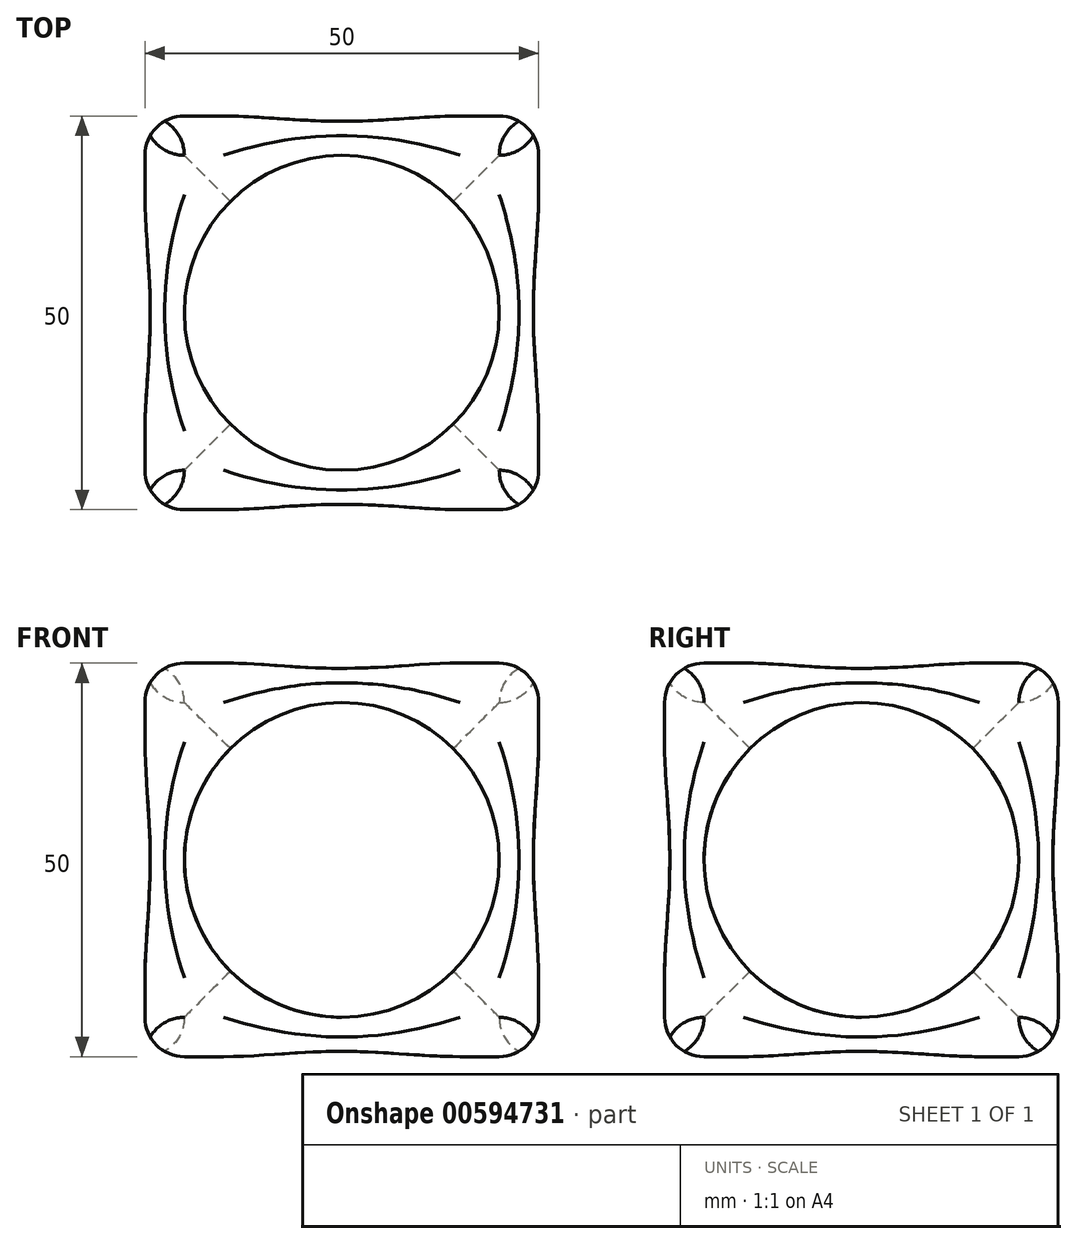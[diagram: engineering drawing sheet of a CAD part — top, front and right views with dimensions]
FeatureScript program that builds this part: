
annotation { "Feature Type Name" : "Feature", "Feature Type Description" : "" }
export const myFeature = defineFeature(function(context is Context, id is Id, definition is map)
    precondition{}
    {
        {
            var Q0;
            Q0=qCreatedBy(makeId("Top.planeOp"),FACE);
            var sketch = newSketch(context, id + "F0", { "sketchPlane" : qUnion([Q0])});
            skLineSegment(sketch, "E0.bottom", {"start": v(0, 0) * mm, "end": v(50, 0) * mm});
            skLineSegment(sketch, "E0.top", {"start": v(0, 50) * mm, "end": v(50, 50) * mm});
            skLineSegment(sketch, "E0.left", {"start": v(0, 0) * mm, "end": v(0, 50) * mm});
            skLineSegment(sketch, "E0.right", {"start": v(50, 0) * mm, "end": v(50, 50) * mm});
            skSolve(sketch);
        }
        {
            var Q0;
            Q0 = qSketchRegion(id + "F0", true);
            extrude(context, id + "F1", {"entities" : qUnion([Q0]), "depth" : 50 * mm, "offsetDistance" : 25 * mm});
        }
        {
            var Q0;
            Q0=makeQuery(id+"F1.opExtrude","SWEPT_FACE",FACE,{"disambiguationData":[OSD([sQuery(id+"F0.wireOp",EDGE,"E0.bottom")])]});
            var sketch = newSketch(context, id + "F2", { "sketchPlane" : qUnion([Q0])});
            skCircle(sketch, "E1", {"center": v(25, 25) * mm, "radius": 20 * mm});
            skSolve(sketch);
        }
        {
            var Q0;
            Q0=makeQuery(id+"F2.imprint","IMPRINT",FACE,{"disambiguationData":[TD([[makeQuery(id+"F2.imprint","IMPRINT",EDGE,{"derivedFrom":sQuery(id+"F2.wireOp",EDGE,"E1")}),1.0]])]});
            extrude(context, id + "F3", {"entities" : qUnion([Q0]), "operationType" : NewBodyOperationType.REMOVE, "oppositeDirection" : true, "depth" : 50 * mm, "offsetDistance" : 25 * mm});
        }
        {
            var Q0;
            Q0=makeQuery(id+"F1.opExtrude","SWEPT_FACE",FACE,{"disambiguationData":[OSD([sQuery(id+"F0.wireOp",EDGE,"E0.right")])]});
            var sketch = newSketch(context, id + "F4", { "sketchPlane" : qUnion([Q0])});
            skCircle(sketch, "E2", {"center": v(25, 25) * mm, "radius": 20 * mm});
            skSolve(sketch);
        }
        {
            var Q0;
            Q0=makeQuery(id+"F4.imprint","IMPRINT",FACE,{"disambiguationData":[TD([[makeQuery(id+"F4.imprint","IMPRINT",EDGE,{"derivedFrom":sQuery(id+"F4.wireOp",EDGE,"E2")}),1.0]])]});
            extrude(context, id + "F5", {"entities" : qUnion([Q0]), "operationType" : NewBodyOperationType.REMOVE, "oppositeDirection" : true, "depth" : 50 * mm, "offsetDistance" : 25 * mm});
        }
        {
            var Q0;
            Q0=makeQuery(id+"F1.opExtrude","CAP_FACE",FACE,{"disambiguationData":[OSD([sQuery(id+"F0.wireOp",EDGE,"E0.bottom"),sQuery(id+"F0.wireOp",EDGE,"E0.top"),sQuery(id+"F0.wireOp",EDGE,"E0.left"),sQuery(id+"F0.wireOp",EDGE,"E0.right")])],"isStart":false});
            var sketch = newSketch(context, id + "F6", { "sketchPlane" : qUnion([Q0])});
            skCircle(sketch, "E3", {"center": v(25, 25) * mm, "radius": 20 * mm});
            skSolve(sketch);
        }
        {
            var Q0;
            Q0 = qSketchRegion(id + "F6", true);
            extrude(context, id + "F7", {"entities" : qUnion([Q0]), "operationType" : NewBodyOperationType.REMOVE, "oppositeDirection" : true, "depth" : 50 * mm, "offsetDistance" : 25 * mm});
        }
        {
            var Q0;
            Q0=makeQuery(id+"F7.boolean.opBoolean","COPY",EDGE,{"derivedFrom":makeQuery(id+"F7.opExtrude","CAP_EDGE",EDGE,{"disambiguationData":[OSD([sQuery(id+"F6.wireOp",EDGE,"E3")])],"isStart":true})});
            var Q1;
            Q1=makeQuery(id+"F1.opExtrude","CAP_FACE",FACE,{"disambiguationData":[OSD([sQuery(id+"F0.wireOp",EDGE,"E0.bottom"),sQuery(id+"F0.wireOp",EDGE,"E0.top"),sQuery(id+"F0.wireOp",EDGE,"E0.left"),sQuery(id+"F0.wireOp",EDGE,"E0.right")])],"isStart":false});
            var Q2;
            Q2=makeQuery(id+"F1.opExtrude","SWEPT_FACE",FACE,{"disambiguationData":[OSD([sQuery(id+"F0.wireOp",EDGE,"E0.right")])]});
            var Q3;
            Q3=makeQuery(id+"F1.opExtrude","SWEPT_FACE",FACE,{"disambiguationData":[OSD([sQuery(id+"F0.wireOp",EDGE,"E0.bottom")])]});
            var Q4;
            Q4=makeQuery(id+"F1.opExtrude","SWEPT_FACE",FACE,{"disambiguationData":[OSD([sQuery(id+"F0.wireOp",EDGE,"E0.left")])]});
            var Q5;
            Q5=makeQuery(id+"F1.opExtrude","SWEPT_FACE",FACE,{"disambiguationData":[OSD([sQuery(id+"F0.wireOp",EDGE,"E0.top")])]});
            var Q6;
            Q6=makeQuery(id+"F1.opExtrude","CAP_FACE",FACE,{"disambiguationData":[OSD([sQuery(id+"F0.wireOp",EDGE,"E0.bottom"),sQuery(id+"F0.wireOp",EDGE,"E0.top"),sQuery(id+"F0.wireOp",EDGE,"E0.left"),sQuery(id+"F0.wireOp",EDGE,"E0.right")])],"isStart":true});
            fillet(context, id + "F8", {"entities" : qUnion([Q0, Q1, Q2, Q3, Q4, Q5, Q6]), "radius" : 5 * mm, "tangentPropagation" : true, "allowEdgeOverflow" : false});
        }
    });
